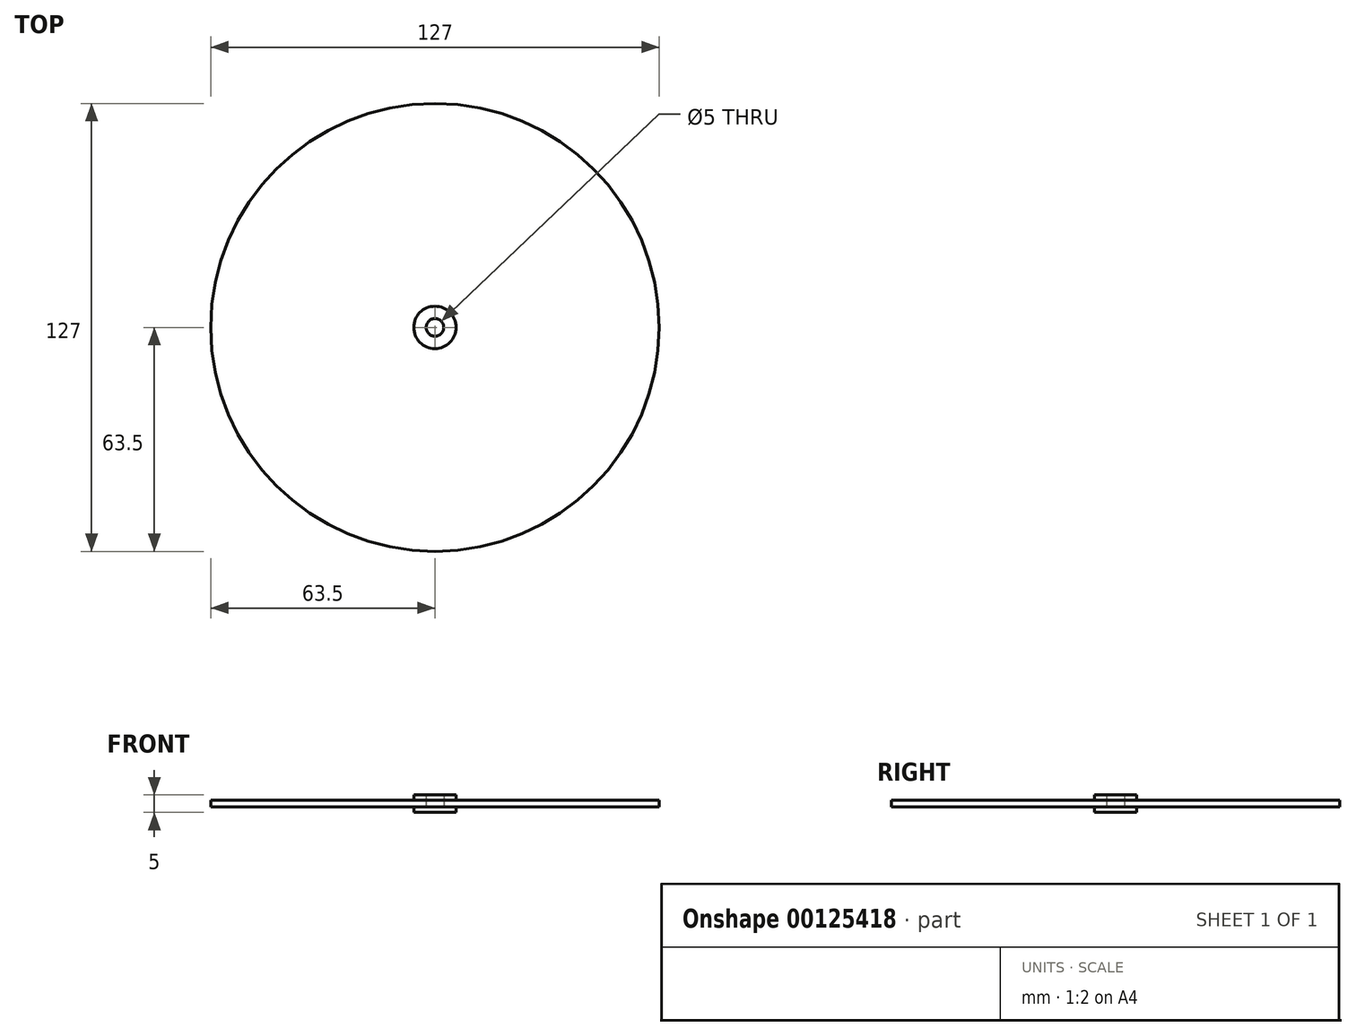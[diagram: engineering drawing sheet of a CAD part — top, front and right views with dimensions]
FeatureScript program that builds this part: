
annotation { "Feature Type Name" : "Feature", "Feature Type Description" : "" }
export const myFeature = defineFeature(function(context is Context, id is Id, definition is map)
    precondition{}
    {
        {
            var Q0;
            Q0=qCreatedBy(makeId("Top.planeOp"),FACE);
            var sketch = newSketch(context, id + "F0", { "sketchPlane" : qUnion([Q0])});
            skCircle(sketch, "E0", {"center": v(0, 0) * mm, "radius": 2.5 * mm});
            skCircle(sketch, "E1", {"center": v(0, 0) * mm, "radius": 6 * mm});
            skSolve(sketch);
        }
        {
            var Q0;
            Q0=makeQuery(id+"F0.imprint","IMPRINT",FACE,{"disambiguationData":[TD([[makeQuery(id+"F0.imprint","IMPRINT",EDGE,{"derivedFrom":sQuery(id+"F0.wireOp",EDGE,"E0")}),-1.0]])]});
            extrude(context, id + "F1", {"entities" : qUnion([Q0]), "endBound" : BoundingType.SYMMETRIC, "depth" : 5 * mm});
        }
        {
            var Q0;
            Q0=qCreatedBy(makeId("Top.planeOp"),FACE);
            var sketch = newSketch(context, id + "F2", { "sketchPlane" : qUnion([Q0])});
            skCircle(sketch, "E2", {"center": v(0, 0) * mm, "radius": 63.5 * mm});
            skCircle(sketch, "E3", {"center": v(0, 0) * mm, "radius": 5 * mm});
            skSolve(sketch);
        }
        {
            var Q0;
            Q0=makeQuery(id+"F2.imprint","IMPRINT",FACE,{"disambiguationData":[TD([[makeQuery(id+"F2.imprint","IMPRINT",EDGE,{"derivedFrom":sQuery(id+"F2.wireOp",EDGE,"E2")}),1.0]])]});
            extrude(context, id + "F3", {"entities" : qUnion([Q0]), "operationType" : NewBodyOperationType.ADD, "endBound" : BoundingType.SYMMETRIC, "depth" : 2 * mm});
        }
    });
